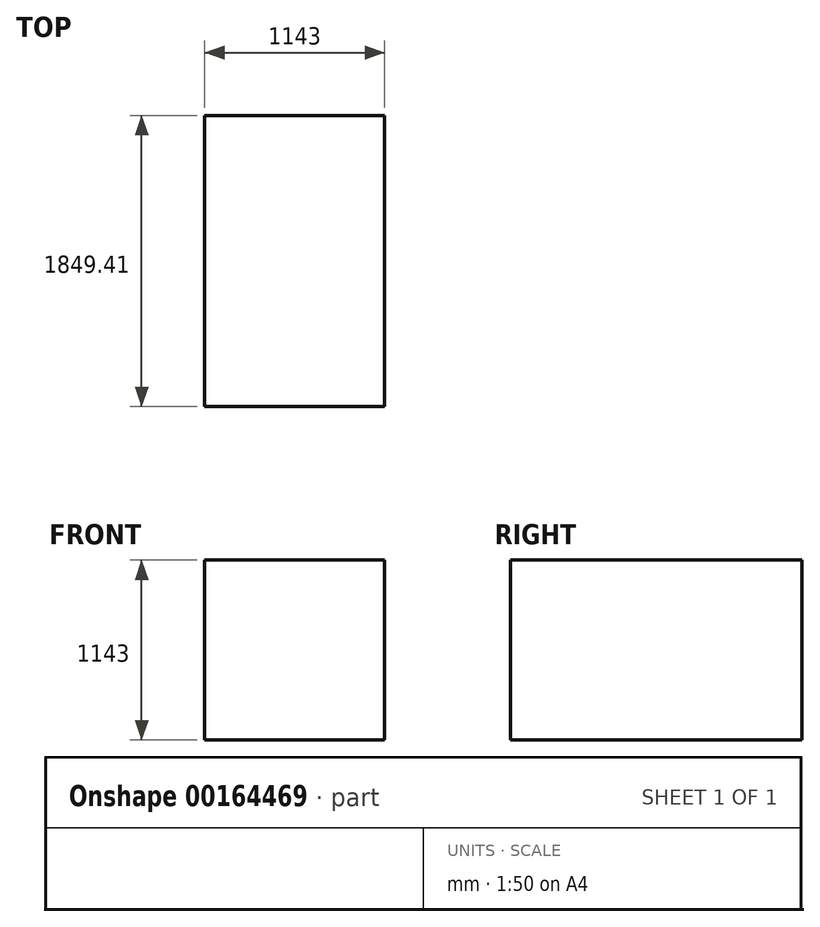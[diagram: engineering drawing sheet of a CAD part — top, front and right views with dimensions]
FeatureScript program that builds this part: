
annotation { "Feature Type Name" : "Feature", "Feature Type Description" : "" }
export const myFeature = defineFeature(function(context is Context, id is Id, definition is map)
    precondition{}
    {
        {
            var Q0;
            Q0=qCreatedBy(makeId("Front.planeOp"),FACE);
            var sketch = newSketch(context, id + "F0", { "sketchPlane" : qUnion([Q0])});
            skLineSegment(sketch, "E0.bottom", {"start": v(-571.5, 571.5) * mm, "end": v(571.5, 571.5) * mm});
            skLineSegment(sketch, "E0.top", {"start": v(-571.5, -571.5) * mm, "end": v(571.5, -571.5) * mm});
            skLineSegment(sketch, "E0.left", {"start": v(-571.5, 571.5) * mm, "end": v(-571.5, -571.5) * mm});
            skLineSegment(sketch, "E0.right", {"start": v(571.5, 571.5) * mm, "end": v(571.5, -571.5) * mm});
            skPoint(sketch, "E0.middle", {"position": v(0, 0) * mm});
            skSolve(sketch);
        }
        {
            var Q0;
            Q0 = qSketchRegion(id + "F0", true);
            extrude(context, id + "F1", {"entities" : qUnion([Q0]), "depth" : 1849.4 * mm});
        }
    });
